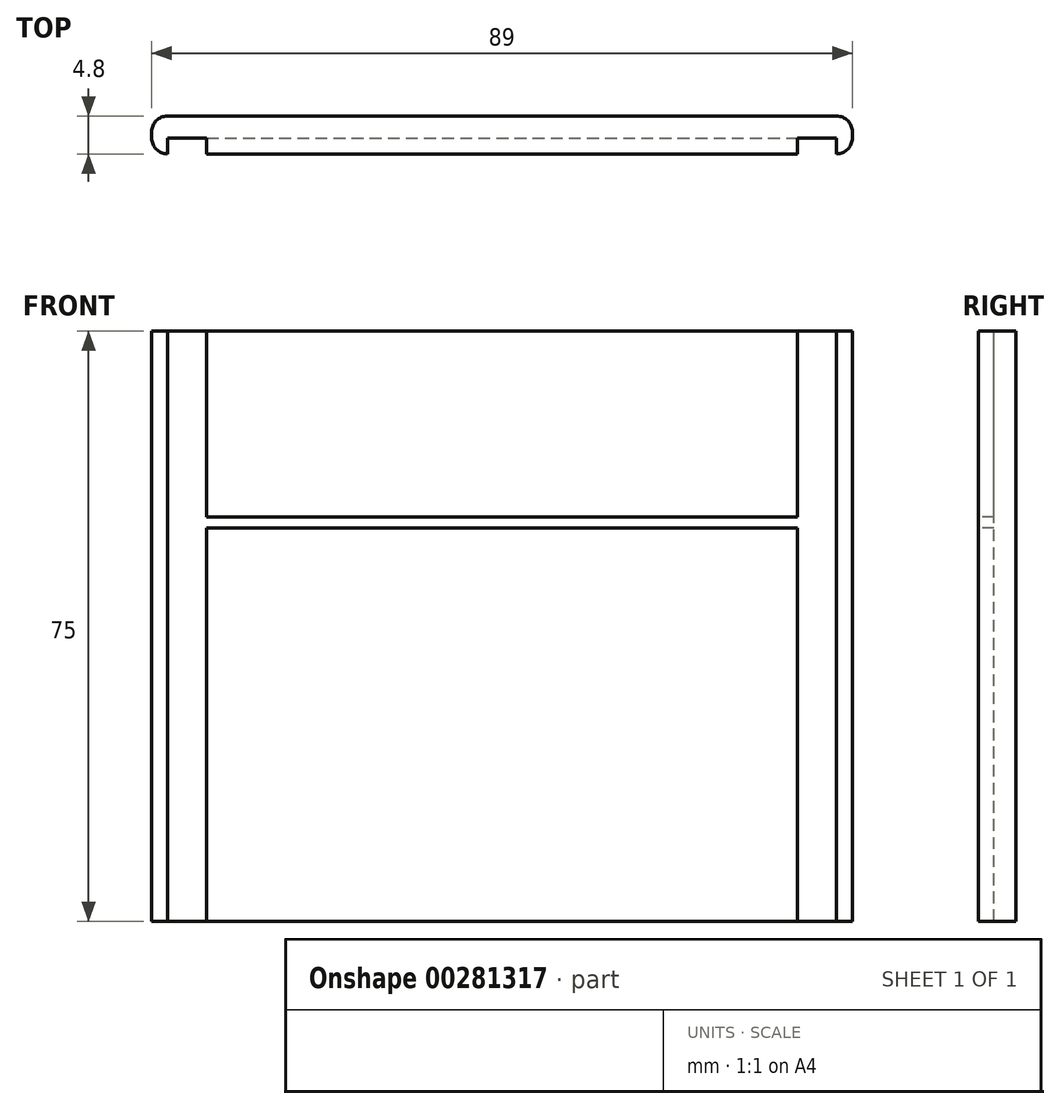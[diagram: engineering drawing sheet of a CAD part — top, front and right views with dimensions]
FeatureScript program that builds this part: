
annotation { "Feature Type Name" : "Feature", "Feature Type Description" : "" }
export const myFeature = defineFeature(function(context is Context, id is Id, definition is map)
    precondition{}
    {
        {
            var Q0;
            Q0=qCreatedBy(makeId("Front.planeOp"),FACE);
            var sketch = newSketch(context, id + "F0", { "sketchPlane" : qUnion([Q0])});
            skLineSegment(sketch, "E0.bottom", {"start": v(44.5, -37.5) * mm, "end": v(-44.5, -37.5) * mm});
            skLineSegment(sketch, "E0.top", {"start": v(44.5, 37.5) * mm, "end": v(-44.5, 37.5) * mm});
            skLineSegment(sketch, "E0.left", {"start": v(44.5, -37.5) * mm, "end": v(44.5, 37.5) * mm});
            skLineSegment(sketch, "E0.right", {"start": v(-44.5, -37.5) * mm, "end": v(-44.5, 37.5) * mm});
            skPoint(sketch, "E0.middle", {"position": v(0, 0) * mm});
            skSolve(sketch);
        }
        {
            var Q0;
            Q0 = qSketchRegion(id + "F0", true);
            extrude(context, id + "F1", {"entities" : qUnion([Q0]), "depth" : 4.8 * mm});
        }
        {
            var Q0;
            Q0=makeQuery(id+"F1.opExtrude","CAP_FACE",FACE,{"disambiguationData":[OSD([sQuery(id+"F0.wireOp",EDGE,"E0.bottom"),sQuery(id+"F0.wireOp",EDGE,"E0.top"),sQuery(id+"F0.wireOp",EDGE,"E0.left"),sQuery(id+"F0.wireOp",EDGE,"E0.right")])],"isStart":false});
            var sketch = newSketch(context, id + "F2", { "sketchPlane" : qUnion([Q0])});
            skPoint(sketch, "E1.middle", {"position": v(0, 13.2) * mm});
            skLineSegment(sketch, "E2.bottom", {"start": v(-42.5, -37.5) * mm, "end": v(-37.5, -37.5) * mm});
            skLineSegment(sketch, "E2.top", {"start": v(-42.5, 37.5) * mm, "end": v(-37.5, 37.5) * mm});
            skLineSegment(sketch, "E2.left", {"start": v(-42.5, -37.5) * mm, "end": v(-42.5, 37.5) * mm});
            skLineSegment(sketch, "E2.right", {"start": v(-37.5, -37.5) * mm, "end": v(-37.5, 37.5) * mm});
            skPoint(sketch, "E2.middle", {"position": v(-40, 0) * mm});
            skLineSegment(sketch, "E3.bottom", {"start": v(37.5, -37.5) * mm, "end": v(42.5, -37.5) * mm});
            skLineSegment(sketch, "E3.top", {"start": v(37.5, 37.5) * mm, "end": v(42.5, 37.5) * mm});
            skLineSegment(sketch, "E3.left", {"start": v(37.5, -37.5) * mm, "end": v(37.5, 37.5) * mm});
            skLineSegment(sketch, "E3.right", {"start": v(42.5, -37.5) * mm, "end": v(42.5, 37.5) * mm});
            skPoint(sketch, "E3.middle", {"position": v(40, 0) * mm});
            skPoint(sketch, "E3.middle.positionSnap0", {"position": v(-37.5, 0) * mm});
            skPoint(sketch, "E3.centerSnap0", {"position": v(-37.5, 0) * mm});
            skLineSegment(sketch, "E4.bottom", {"start": v(-37.5, 12.5) * mm, "end": v(37.5, 12.5) * mm});
            skLineSegment(sketch, "E4.top", {"start": v(-37.5, 13.9) * mm, "end": v(37.5, 13.9) * mm});
            skLineSegment(sketch, "E4.left", {"start": v(-37.5, 12.5) * mm, "end": v(-37.5, 13.9) * mm});
            skLineSegment(sketch, "E4.right", {"start": v(37.5, 12.5) * mm, "end": v(37.5, 13.9) * mm});
            skSolve(sketch);
        }
        {
            var Q0;
            Q0 = qSketchRegion(id + "F2", true);
            extrude(context, id + "F3", {"entities" : qUnion([Q0]), "operationType" : NewBodyOperationType.REMOVE, "oppositeDirection" : true, "depth" : 2 * mm});
        }
        {
            var Q0;
            {var subQ0=sQuery(id+"F0.wireOp",EDGE,"E0.right");var subQ1=sQuery(id+"F0.wireOp",EDGE,"E0.top");var subQ3=makeQuery(id+"F1.opExtrude","CAP_EDGE",EDGE,{"disambiguationData":[OSD([subQ0])],"isStart":false});Q0=makeQuery(id+"F3.boolean.opBoolean","SPLIT",EDGE,{"disambiguationData":[TD([makeQuery(id+"F1.opExtrude","SWEPT_FACE",FACE,{"disambiguationData":[OSD([subQ1])]})])],"derivedFrom":subQ3});}
            var Q1;
            {var subQ0=sQuery(id+"F0.wireOp",EDGE,"E0.bottom");var subQ1=sQuery(id+"F0.wireOp",EDGE,"E0.right");var subQ3=makeQuery(id+"F1.opExtrude","CAP_EDGE",EDGE,{"disambiguationData":[OSD([subQ1])],"isStart":false});Q1=makeQuery(id+"F3.boolean.opBoolean","SPLIT",EDGE,{"disambiguationData":[TD([makeQuery(id+"F1.opExtrude","SWEPT_FACE",FACE,{"disambiguationData":[OSD([subQ0])]})])],"derivedFrom":subQ3});}
            var Q2;
            {var subQ0=sQuery(id+"F0.wireOp",EDGE,"E0.left");var subQ1=sQuery(id+"F0.wireOp",EDGE,"E0.top");var subQ3=makeQuery(id+"F1.opExtrude","CAP_EDGE",EDGE,{"disambiguationData":[OSD([subQ0])],"isStart":false});Q2=makeQuery(id+"F3.boolean.opBoolean","SPLIT",EDGE,{"disambiguationData":[TD([makeQuery(id+"F1.opExtrude","SWEPT_FACE",FACE,{"disambiguationData":[OSD([subQ1])]})])],"derivedFrom":subQ3});}
            var Q3;
            {var subQ0=sQuery(id+"F0.wireOp",EDGE,"E0.bottom");var subQ1=sQuery(id+"F0.wireOp",EDGE,"E0.left");var subQ3=makeQuery(id+"F1.opExtrude","CAP_EDGE",EDGE,{"disambiguationData":[OSD([subQ1])],"isStart":false});Q3=makeQuery(id+"F3.boolean.opBoolean","SPLIT",EDGE,{"disambiguationData":[TD([makeQuery(id+"F1.opExtrude","SWEPT_FACE",FACE,{"disambiguationData":[OSD([subQ0])]})])],"derivedFrom":subQ3});}
            var Q4;
            Q4=makeQuery(id+"F1.opExtrude","CAP_EDGE",EDGE,{"disambiguationData":[OSD([sQuery(id+"F0.wireOp",EDGE,"E0.left")])],"isStart":true});
            var Q5;
            Q5=makeQuery(id+"F1.opExtrude","CAP_EDGE",EDGE,{"disambiguationData":[OSD([sQuery(id+"F0.wireOp",EDGE,"E0.right")])],"isStart":true});
            fillet(context, id + "F4", {"entities" : qUnion([Q0, Q1, Q2, Q3, Q4, Q5]), "radius" : 2 * mm, "tangentPropagation" : true, "allowEdgeOverflow" : false});
        }
    });
